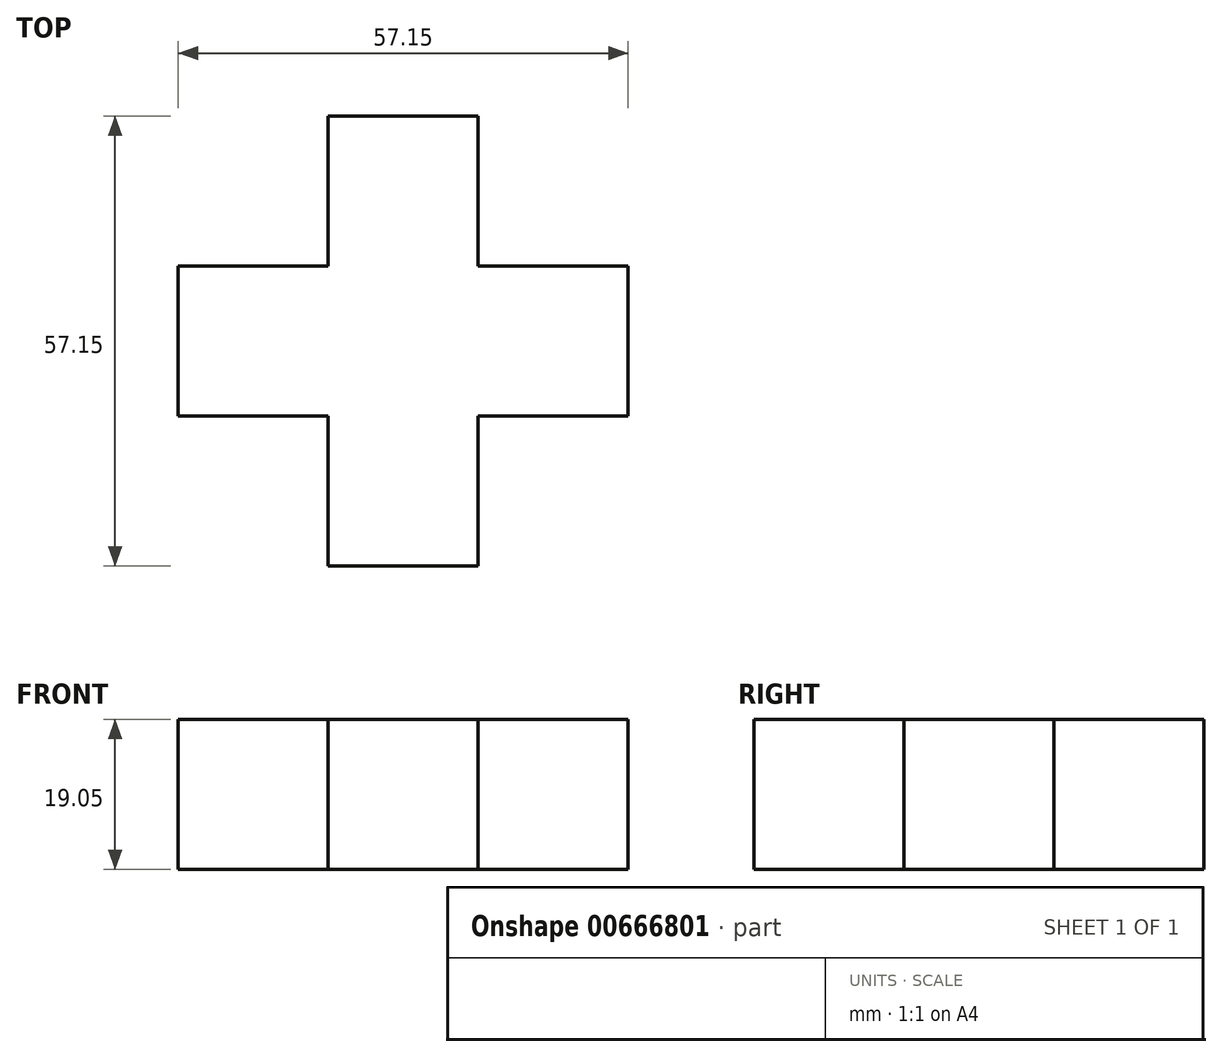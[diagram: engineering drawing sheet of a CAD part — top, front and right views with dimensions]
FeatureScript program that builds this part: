
annotation { "Feature Type Name" : "Feature", "Feature Type Description" : "" }
export const myFeature = defineFeature(function(context is Context, id is Id, definition is map)
    precondition{}
    {
        {
            var Q0;
            Q0=qCreatedBy(makeId("Top.planeOp"),FACE);
            var sketch = newSketch(context, id + "F0", { "sketchPlane" : qUnion([Q0])});
            skLineSegment(sketch, "E0", {"start": v(0, 0) * mm, "end": v(19.05, 0) * mm});
            skLineSegment(sketch, "E1", {"start": v(19.05, 0) * mm, "end": v(19.05, -19.05) * mm});
            skLineSegment(sketch, "E2", {"start": v(19.05, -19.05) * mm, "end": v(38.1, -19.05) * mm});
            skLineSegment(sketch, "E3", {"start": v(38.1, -19.05) * mm, "end": v(38.1, 0) * mm});
            skLineSegment(sketch, "E4", {"start": v(38.1, 0) * mm, "end": v(57.15, 0) * mm});
            skLineSegment(sketch, "E5", {"start": v(57.15, 0) * mm, "end": v(57.15, 19.05) * mm});
            skLineSegment(sketch, "E6", {"start": v(57.15, 19.05) * mm, "end": v(38.1, 19.05) * mm});
            skLineSegment(sketch, "E7", {"start": v(38.1, 19.05) * mm, "end": v(38.1, 38.1) * mm});
            skLineSegment(sketch, "E8", {"start": v(38.1, 38.1) * mm, "end": v(19.05, 38.1) * mm});
            skLineSegment(sketch, "E9", {"start": v(19.05, 38.1) * mm, "end": v(19.05, 19.05) * mm});
            skLineSegment(sketch, "E10", {"start": v(19.05, 19.05) * mm, "end": v(0, 19.05) * mm});
            skLineSegment(sketch, "E11", {"start": v(0, 19.05) * mm, "end": v(0, 0) * mm});
            skSolve(sketch);
        }
        {
            var Q0;
            Q0=makeQuery(id+"F0.imprint","IMPRINT",FACE,{"disambiguationData":[TD([[makeQuery(id+"F0.imprint","IMPRINT",EDGE,{"derivedFrom":sQuery(id+"F0.wireOp",EDGE,"E0")}),1.0]])]});
            extrude(context, id + "F1", {"entities" : qUnion([Q0]), "depth" : 19.05 * mm, "offsetDistance" : 25.4 * mm});
        }
    });
